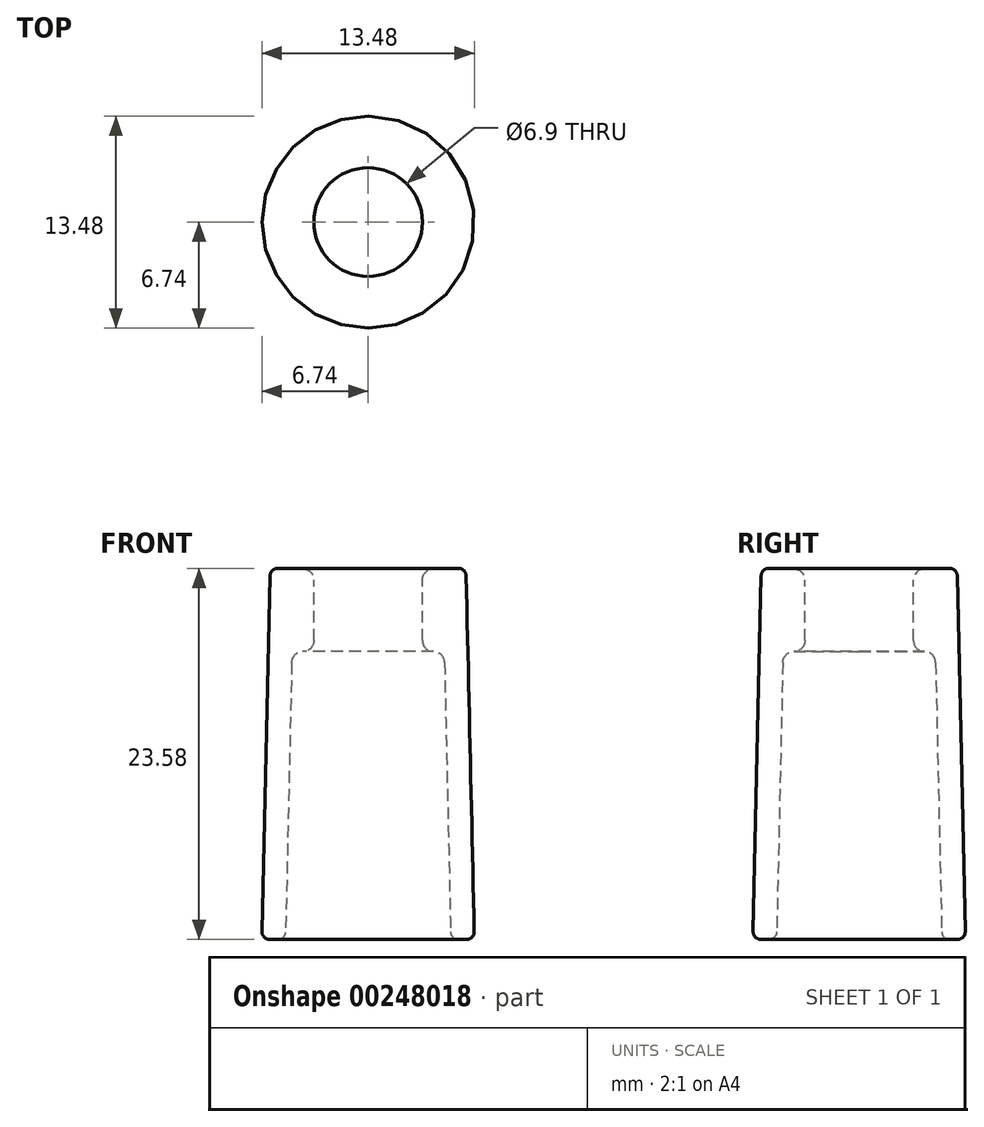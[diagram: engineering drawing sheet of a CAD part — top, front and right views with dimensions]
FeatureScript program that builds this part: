
annotation { "Feature Type Name" : "Feature", "Feature Type Description" : "" }
export const myFeature = defineFeature(function(context is Context, id is Id, definition is map)
    precondition{}
    {
        {
            var Q0;
            Q0=qCreatedBy(makeId("Top.planeOp"),FACE);
            var sketch = newSketch(context, id + "F0", { "sketchPlane" : qUnion([Q0])});
            skCircle(sketch, "E0", {"center": v(0, 0) * mm, "radius": 14.55 * mm});
            skSolve(sketch);
        }
        {
            var Q0;
            Q0=qCreatedBy(makeId("Front.planeOp"),FACE);
            var sketch = newSketch(context, id + "F1", { "sketchPlane" : qUnion([Q0])});
            skLineSegment(sketch, "E1", {"start": v(-5.25, 0) * mm, "end": v(-4.72, 23.56) * mm});
            skLineSegment(sketch, "E2", {"start": v(0, 28.45) * mm, "end": v(0, -26.15) * mm, "construction": true});
            skPoint(sketch, "E3.orphan", {"position": v(-4.9, 15.5) * mm});
            skLineSegment(sketch, "E4", {"start": v(-4.72, 23.56) * mm, "end": v(-6.22, 23.6) * mm});
            skLineSegment(sketch, "E5", {"start": v(-6.22, 23.6) * mm, "end": v(-6.75, 0) * mm});
            skLineSegment(sketch, "E6", {"start": v(-6.75, 0) * mm, "end": v(-5.25, 0) * mm});
            skLineSegment(sketch, "E7", {"start": v(-4.72, 23.56) * mm, "end": v(-3.45, 23.53) * mm});
            skLineSegment(sketch, "E8", {"start": v(-3.45, 23.53) * mm, "end": v(-3.45, 18.28) * mm});
            skLineSegment(sketch, "E9", {"start": v(-3.45, 18.28) * mm, "end": v(-4.84, 18.28) * mm});
            skLineSegment(sketch, "E10.MirrorCS", {"start": v(4.67, 16.87) * mm, "end": v(5.3, 0.92) * mm});
            skFitSpline(sketch, "E11", {"points": [v(-5.14, 4.68) * mm, v(-4.75, -0.63) * mm, v(-6.75, 0) * mm], "startDerivative": vector(-0.45, -19.86) * mm, "endDerivative": vector(0.14, 6.18) * mm});
            skLineSegment(sketch, "E12", {"start": v(-2.4, 4.43) * mm, "end": v(-2.4, 1.06) * mm, "construction": true});
            skSolve(sketch);
        }
        {
            var Q0;
            {var subQ0=sQuery(id+"F1.wireOp",EDGE,"E4");Q0=makeQuery(id+"F1.imprint","IMPRINT",FACE,{"disambiguationData":[TD([[makeQuery(id+"F1.imprint","IMPRINT",EDGE,{"derivedFrom":subQ0}),1.0]])]});}
            var Q1;
            {var subQ0=sQuery(id+"F1.wireOp",EDGE,"E7");Q1=makeQuery(id+"F1.imprint","IMPRINT",FACE,{"disambiguationData":[TD([[makeQuery(id+"F1.imprint","IMPRINT",EDGE,{"derivedFrom":subQ0}),-1.0]])]});}
            var Q2;
            Q2=sQuery(id+"F1.wireOp",EDGE,"E2");
            revolve(context, id + "F2", {"entities" : qUnion([Q0, Q1]), "axis" : qUnion([Q2]), "revolveType" : RevolveType.FULL});
        }
        {
            var Q0;
            Q0=makeQuery(id+"F2.opRevolve","SWEPT_EDGE",EDGE,{"disambiguationData":[OSD([sQuery(id+"F1.wireOp",EDGE,"E4"),sQuery(id+"F1.wireOp",EDGE,"E5")])]});
            var Q1;
            Q1=makeQuery(id+"F2.opRevolve","SWEPT_FACE",FACE,{"disambiguationData":[OSD([sQuery(id+"F1.wireOp",EDGE,"E6")])]});
            fillet(context, id + "F3", {"entities" : qUnion([Q0, Q1]), "radius" : .5 * mm, "tangentPropagation" : true, "allowEdgeOverflow" : false});
        }
        {
            var Q0;
            Q0=makeQuery(id+"F2.opRevolve","SWEPT_FACE",FACE,{"disambiguationData":[OSD([sQuery(id+"F1.wireOp",EDGE,"E8")])]});
            var Q1;
            Q1=makeQuery(id+"F2.opRevolve","SWEPT_EDGE",EDGE,{"disambiguationData":[OSD([sQuery(id+"F1.wireOp",EDGE,"E1"),sQuery(id+"F1.wireOp",EDGE,"E9")])]});
            fillet(context, id + "F4", {"entities" : qUnion([Q0, Q1]), "radius" : .70 * mm, "tangentPropagation" : true, "allowEdgeOverflow" : false});
        }
    });
